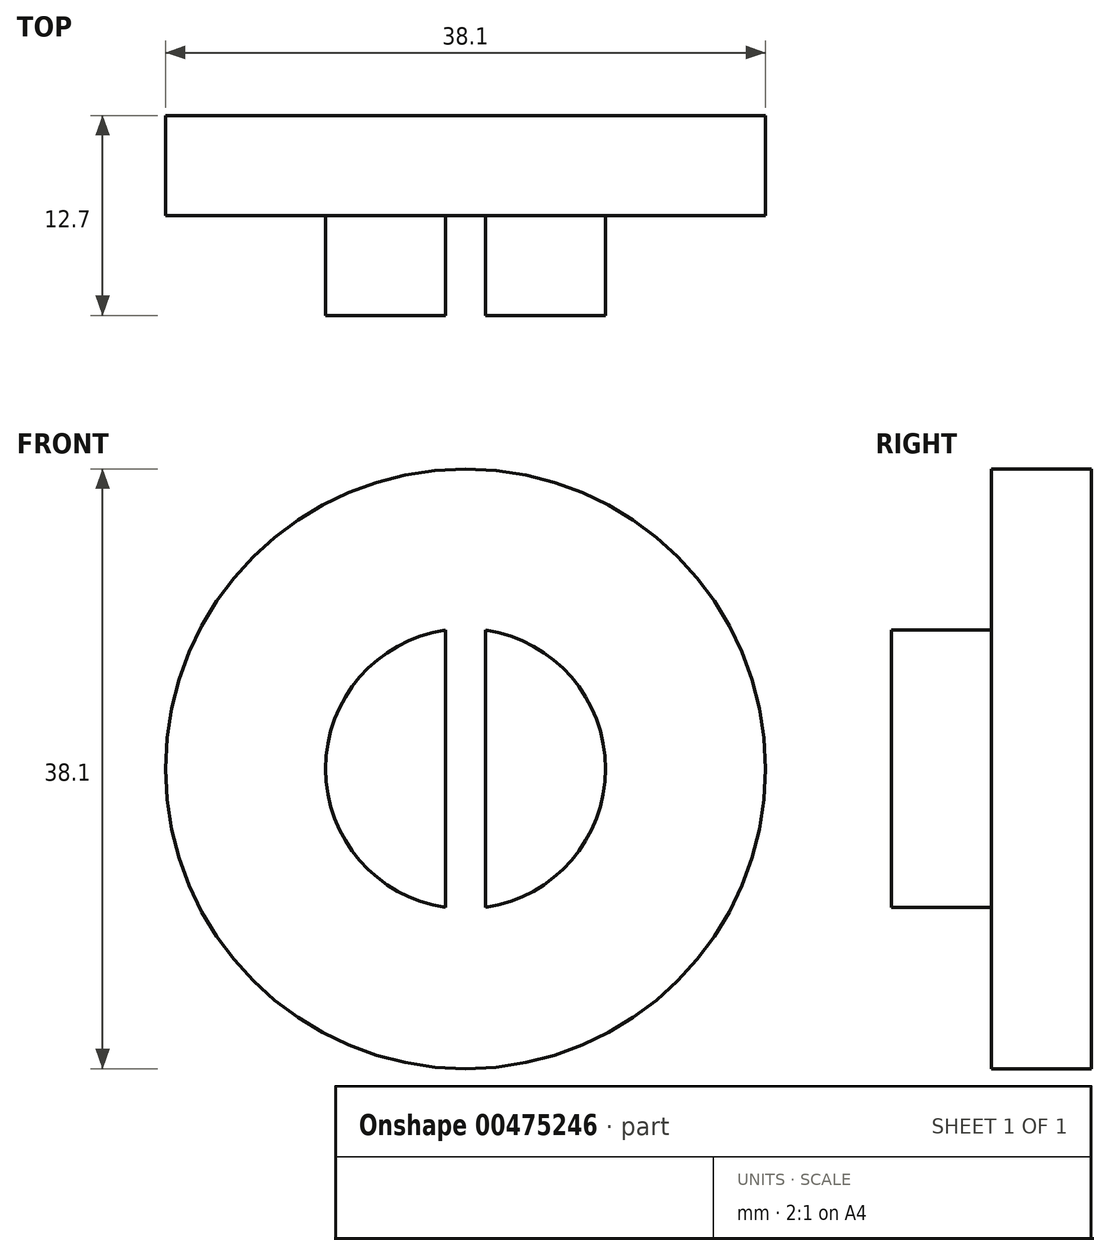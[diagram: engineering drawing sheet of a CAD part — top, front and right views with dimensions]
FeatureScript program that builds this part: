
annotation { "Feature Type Name" : "Feature", "Feature Type Description" : "" }
export const myFeature = defineFeature(function(context is Context, id is Id, definition is map)
    precondition{}
    {
        {
            var Q0;
            Q0=qCreatedBy(makeId("Front.planeOp"),FACE);
            var sketch = newSketch(context, id + "F0", { "sketchPlane" : qUnion([Q0])});
            skCircle(sketch, "E0", {"center": v(0, 0) * mm, "radius": 19.05 * mm});
            skSolve(sketch);
        }
        {
            var Q0;
            Q0=makeQuery(id+"F0.imprint","IMPRINT",FACE,{"disambiguationData":[TD([[makeQuery(id+"F0.imprint","IMPRINT",EDGE,{"derivedFrom":sQuery(id+"F0.wireOp",EDGE,"E0")}),1.0]])]});
            extrude(context, id + "F1", {"entities" : qUnion([Q0]), "depth" : 6.35 * mm});
        }
        {
            var Q0;
            Q0=qCreatedBy(makeId("Front.planeOp"),FACE);
            var sketch = newSketch(context, id + "F2", { "sketchPlane" : qUnion([Q0])});
            skLineSegment(sketch, "E1", {"start": v(-1.27, 8.8) * mm, "end": v(-1.27, -8.8) * mm});
            skLineSegment(sketch, "E2", {"start": v(1.27, 8.8) * mm, "end": v(1.27, -8.8) * mm});
            skArc(sketch, "E3", {"start": v(-1.27, 8.8) * mm, "mid": v(-8.9, 0) * mm, "end": v(-1.27, -8.8) * mm});
            skArc(sketch, "E4", {"start": v(1.27, -8.8) * mm, "mid": v(8.9, 0) * mm, "end": v(1.27, 8.8) * mm});
            skSolve(sketch);
        }
        {
            var Q0;
            Q0 = qSketchRegion(id + "F2", true);
            extrude(context, id + "F3", {"entities" : qUnion([Q0]), "operationType" : NewBodyOperationType.ADD, "depth" : 38.1 * mm});
        }
        {
            var Q0;
            Q0=makeQuery(id+"F3.opExtrude","CAP_FACE",FACE,{"disambiguationData":[OSD([sQuery(id+"F2.wireOp",EDGE,"E2"),sQuery(id+"F2.wireOp",EDGE,"E4")])],"isStart":false});
            var Q1;
            Q1=makeQuery(id+"F3.opExtrude","CAP_FACE",FACE,{"disambiguationData":[OSD([sQuery(id+"F2.wireOp",EDGE,"E1"),sQuery(id+"F2.wireOp",EDGE,"E3")])],"isStart":false});
            extrude(context, id + "F4", {"entities" : qUnion([Q0, Q1]), "operationType" : NewBodyOperationType.REMOVE, "oppositeDirection" : true, "depth" : 25.4 * mm});
        }
    });
